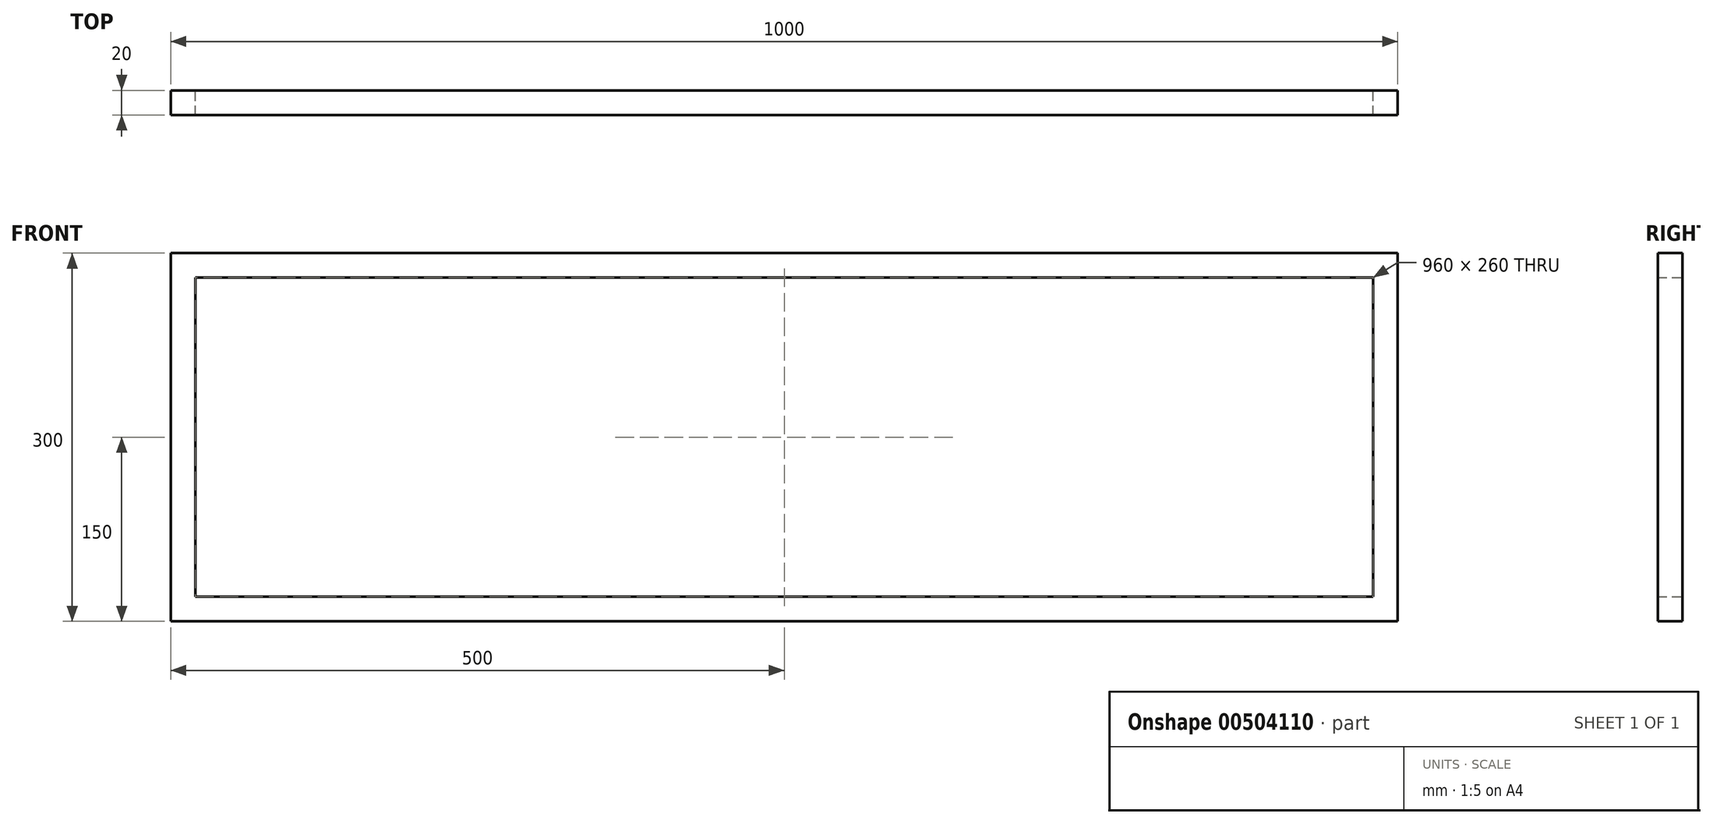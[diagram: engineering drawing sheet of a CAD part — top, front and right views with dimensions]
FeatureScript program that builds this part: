
annotation { "Feature Type Name" : "Feature", "Feature Type Description" : "" }
export const myFeature = defineFeature(function(context is Context, id is Id, definition is map)
    precondition{}
    {
        {
            var Q0;
            Q0=qCreatedBy(makeId("Front.planeOp"),FACE);
            var sketch = newSketch(context, id + "F0", { "sketchPlane" : qUnion([Q0])});
            skLineSegment(sketch, "E0.bottom", {"start": v(0, 0) * mm, "end": v(1000, 0) * mm});
            skLineSegment(sketch, "E0.top", {"start": v(0, 300) * mm, "end": v(1000, 300) * mm});
            skLineSegment(sketch, "E0.left", {"start": v(0, 0) * mm, "end": v(0, 300) * mm});
            skLineSegment(sketch, "E0.right", {"start": v(1000, 0) * mm, "end": v(1000, 300) * mm});
            skSolve(sketch);
        }
        {
            var Q0;
            Q0=qCreatedBy(makeId("Right.planeOp"),FACE);
            var sketch = newSketch(context, id + "F1", { "sketchPlane" : qUnion([Q0])});
            skLineSegment(sketch, "E1.bottom", {"start": v(0, 0) * mm, "end": v(20, 0) * mm});
            skLineSegment(sketch, "E1.top", {"start": v(0, 20) * mm, "end": v(20, 20) * mm});
            skLineSegment(sketch, "E1.left", {"start": v(0, 0) * mm, "end": v(0, 20) * mm});
            skLineSegment(sketch, "E1.right", {"start": v(20, 0) * mm, "end": v(20, 20) * mm});
            skSolve(sketch);
        }
        {
            var Q0;
            Q0=makeQuery(id+"F1.imprint","IMPRINT",FACE,{"disambiguationData":[TD([[makeQuery(id+"F1.imprint","IMPRINT",EDGE,{"derivedFrom":sQuery(id+"F1.wireOp",EDGE,"E1.bottom")}),1.0]])]});
            var Q1;
            Q1=sQuery(id+"F0.wireOp",EDGE,"E0.left");
            var Q2;
            Q2=sQuery(id+"F0.wireOp",EDGE,"E0.bottom");
            var Q3;
            Q3=sQuery(id+"F0.wireOp",EDGE,"E0.top");
            var Q4;
            Q4=sQuery(id+"F0.wireOp",EDGE,"E0.right");
            sweep(context, id + "F2", {"profiles" : qUnion([Q0]), "path" : qUnion([Q1, Q2, Q3, Q4])});
        }
    });
